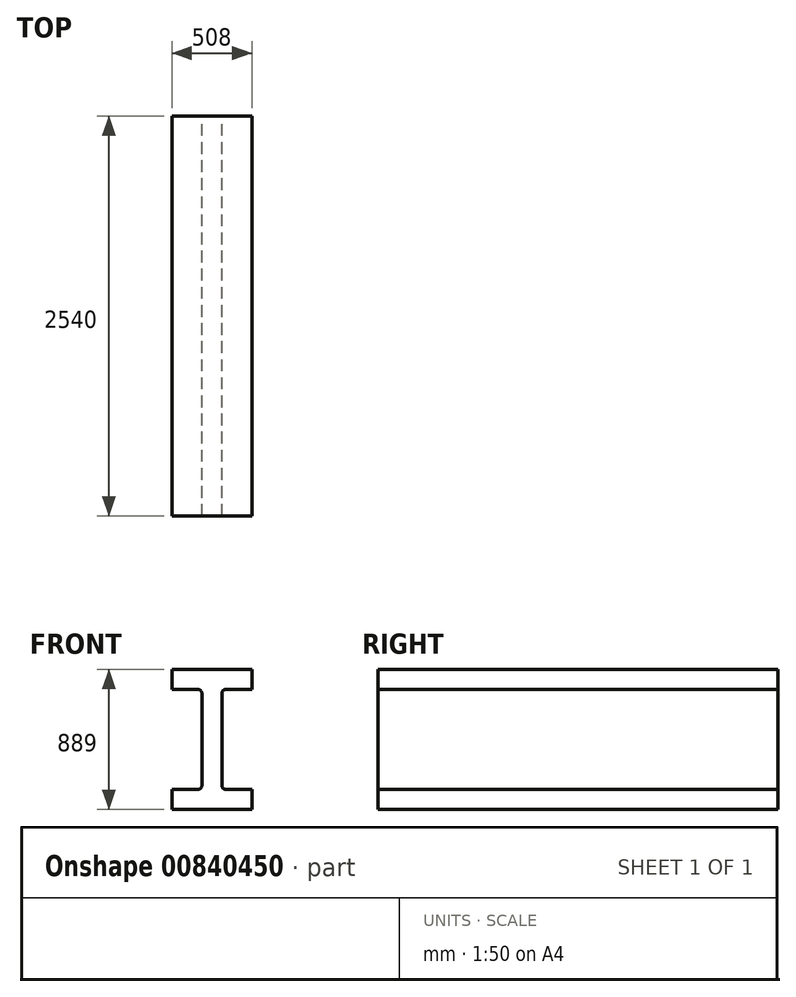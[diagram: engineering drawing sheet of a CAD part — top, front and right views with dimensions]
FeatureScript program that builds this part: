
annotation { "Feature Type Name" : "Feature", "Feature Type Description" : "" }
export const myFeature = defineFeature(function(context is Context, id is Id, definition is map)
    precondition{}
    {
        {
            var Q0;
            Q0=qCreatedBy(makeId("Front.planeOp"),FACE);
            var sketch = newSketch(context, id + "F0", { "sketchPlane" : qUnion([Q0])});
            skLineSegment(sketch, "E0.bottom", {"start": v(-129.9, -82.4) * mm, "end": v(-637.9, -82.4) * mm});
            skLineSegment(sketch, "E0.top", {"start": v(-129.9, 806.6) * mm, "end": v(-637.9, 806.6) * mm});
            skLineSegment(sketch, "E0.left", {"start": v(-129.9, -82.4) * mm, "end": v(-129.9, 44.6) * mm});
            skLineSegment(sketch, "E0.right", {"start": v(-637.9, -82.4) * mm, "end": v(-637.9, 44.6) * mm});
            skPoint(sketch, "E0.middle", {"position": v(-383.9, 362.1) * mm});
            skPoint(sketch, "E1.middle", {"position": v(-637.9, 717.8) * mm});
            skLineSegment(sketch, "E2.bottom", {"start": v(-637.9, 679.6) * mm, "end": v(-472.8, 679.6) * mm});
            skLineSegment(sketch, "E2.top", {"start": v(-637.9, 44.6) * mm, "end": v(-472.8, 44.6) * mm});
            skLineSegment(sketch, "E3.left", {"start": v(-320.4, 70) * mm, "end": v(-320.4, 654.2) * mm});
            skLineSegment(sketch, "E3.right", {"start": v(-447.4, 70) * mm, "end": v(-447.4, 654.2) * mm});
            skLineSegment(sketch, "E4.trimOffspring", {"start": v(-129.9, 679.6) * mm, "end": v(-129.9, 806.6) * mm});
            skLineSegment(sketch, "E5.trimOffspring", {"start": v(-637.9, 679.6) * mm, "end": v(-637.9, 806.6) * mm});
            skLineSegment(sketch, "E6.trimOffspring", {"start": v(-295, 679.6) * mm, "end": v(-129.9, 679.6) * mm});
            skLineSegment(sketch, "E7.trimOffspring", {"start": v(-295, 44.6) * mm, "end": v(-129.9, 44.6) * mm});
            skPoint(sketch, "E8.visualSharp", {"position": v(-320.4, 679.6) * mm});
            skArc(sketch, "E8.filletArc", {"start": v(-295, 679.6) * mm, "mid": v(-312.96, 672.16) * mm, "end": v(-320.4, 654.2) * mm});
            skPoint(sketch, "E9.visualSharp", {"position": v(-447.4, 679.6) * mm});
            skArc(sketch, "E9.filletArc", {"start": v(-447.4, 654.2) * mm, "mid": v(-454.84, 672.16) * mm, "end": v(-472.8, 679.6) * mm});
            skPoint(sketch, "E10.visualSharp", {"position": v(-320.4, 44.6) * mm});
            skArc(sketch, "E10.filletArc", {"start": v(-320.4, 70) * mm, "mid": v(-312.96, 52.03) * mm, "end": v(-295, 44.6) * mm});
            skPoint(sketch, "E11.visualSharp", {"position": v(-447.4, 44.6) * mm});
            skArc(sketch, "E11.filletArc", {"start": v(-472.8, 44.6) * mm, "mid": v(-454.84, 52.03) * mm, "end": v(-447.4, 70) * mm});
            skSolve(sketch);
        }
        {
            var Q0;
            Q0 = qSketchRegion(id + "F0", true);
            extrude(context, id + "F1", {"entities" : qUnion([Q0]), "depth" : 2540 * mm, "offsetDistance" : 25.4 * mm});
        }
    });
